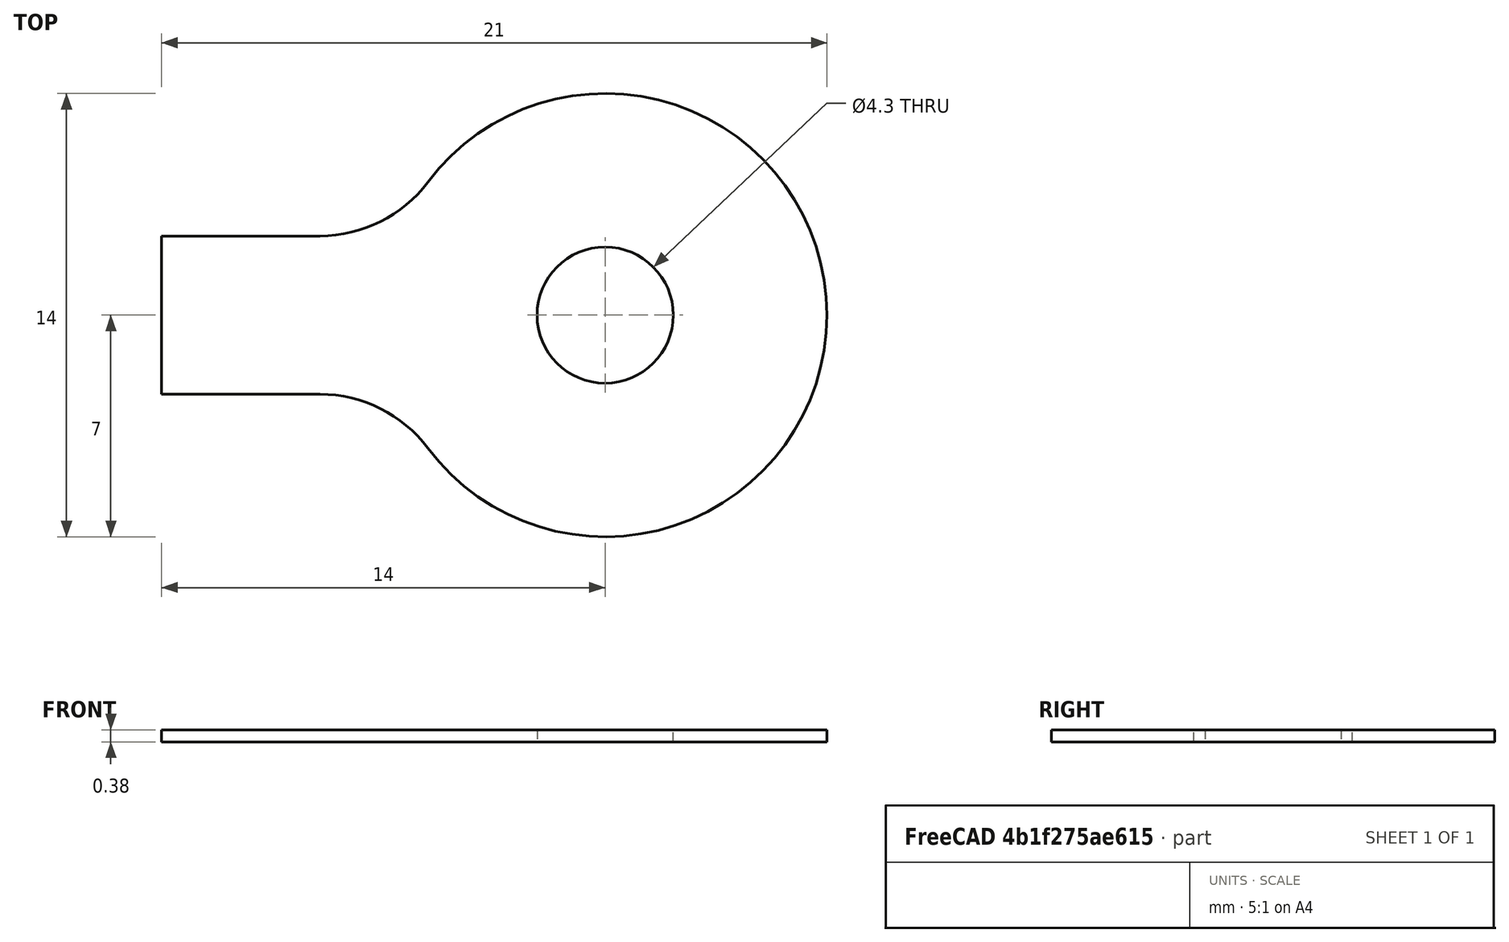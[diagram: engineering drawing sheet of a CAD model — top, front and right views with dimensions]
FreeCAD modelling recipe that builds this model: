
FCSTD DOCUMENT  (FreeCAD 0.15R4671 (Git))
Label: DIN93_M4TabWasher
License: CreativeCommons Attribution-ShareAlike
LicenseURL: http://creativecommons.org/licenses/by-sa/4.0/
objects: Sketcher::SketchObject×1, PartDesign::Pad×1
note: 3 computed .brp shape members not serialized (recipe doc carries the construction recipe); baked Part::Feature solids carry a one-line shape summary decoded from their .brp

FEATURE [Sketcher::SketchObject] Sketch
  sketch-geometry (7):
    g0: Circle CenterX=0 CenterY=0 CenterZ=0 NormalX=0 NormalY=0 NormalZ=1 Radius=2.15
    g1: LineSegment StartX=-14 StartY=2.5 StartZ=0 EndX=-9 EndY=2.5 EndZ=0
    g2: LineSegment StartX=-9 StartY=-2.5 StartZ=0 EndX=-14 EndY=-2.5 EndZ=0
    g3: LineSegment StartX=-14 StartY=-2.5 StartZ=0 EndX=-14 EndY=2.5 EndZ=0
    g4: ArcOfCircle CenterX=0 CenterY=0 CenterZ=0 NormalX=0 NormalY=0 NormalZ=1 Radius=7 StartAngle=3.78509 EndAngle=8.78128
    g5: ArcOfCircle CenterX=-8.99999 CenterY=6.74998 CenterZ=0 NormalX=0 NormalY=0 NormalZ=1 Radius=4.24998 StartAngle=4.71239 EndAngle=5.63969
    g6: ArcOfCircle CenterX=-9 CenterY=-6.75 CenterZ=0 NormalX=0 NormalY=0 NormalZ=1 Radius=4.25 StartAngle=0.643501 EndAngle=1.5708
  constraints (22):
    c: Coincident(g0,g-1)
    c: Radius(g0) = 2.15
    c: Coincident(g2,g3)
    c: Coincident(g3,g1)
    c: Horizontal(g1)
    c: Horizontal(g2)
    c: Vertical(g3)
    c: Symmetric(g1,g2,g-1)
    c: Equal(g1,g3)
    c: Equal(g3,g2)
    c: DistanceY(g3) = 5
    c: DistanceX(g-1,g2) = -14
    c: Coincident(g4,g-1)
    c: Radius(g4) = 7
    c: Coincident(g5,g4)
    c: Coincident(g5,g1)
    c: Tangent(g5,g4)
    c: Coincident(g6,g2)
    c: Coincident(g6,g4)
    c: Tangent(g4,g6)
    c: Tangent(g6,g2)
    c: Tangent(g1,g5)
FEATURE [PartDesign::Pad] Pad
  Length = 0.38
  Length2 = 100
  Sketch = -> Sketch
  Type = 0
